# Revit family: Воздухоудалитель с функцией  выпуска воздуха 2630 10
name_source: partatom
category: Rohrzubehör
units: mm (PartAtom-declared; Revit-internal decimal feet)

## family parameters
Arbeitsebenenbasiert = Nein
Beim Laden mit Abzugskörper schneiden = Nein
Bemaßung runder Anschluss = Durchmesser verwenden
Gemeinsam genutzt = Nein
Immer vertikal = Ja
OmniClass-Nummer = 23.65.55.14
OmniClass-Titel = Valves for Liquid Services
Teiletyp = Normal

## types (1)
- Воздухоудалитель с функцией  выпуска воздуха 2630 10
    D01 = 17.8 mm  [stored 0.0583989 ft]
    D02 = 20 mm  [stored 0.0656168 ft]
    D03 = 11 mm  [stored 0.0360892 ft]
    D04 = 12.5 mm  [stored 0.0410105 ft]
    D05 = 5.1 mm  [stored 0.0167323 ft]
    D06 = 3.4 mm  [stored 0.0111549 ft]
    H00 = 56 mm  [stored 0.183727 ft]
    H01 = 9.5 mm  [stored 0.031168 ft]
    H02 = 13 mm
    H03 = 15.5 mm  [stored 0.050853 ft]
    H04 = 14.5 mm  [stored 0.0475722 ft]
    H05 = 9 mm  [stored 0.0295276 ft]
    H06 = 2.5 mm  [stored 0.0082021 ft]
    H07 = 48.5 mm
    H08 = 55 mm  [stored 0.180446 ft]
    Hersteller = Herz-Armaturen GmbH
    L01 = 4 mm  [stored 0.0131234 ft]
    L02 = 28.3 mm  [stored 0.0928478 ft]
    L03 = 9.5 mm  [stored 0.031168 ft]
    L04 = 18.8 mm  [stored 0.0616798 ft]
    R01 = 1 mm  [stored 0.00328084 ft]
    R02 = 0.6 mm  [stored 0.0019685 ft]
    S01 = 56 mm  [stored 0.183727 ft]
    S02 = 11 mm  [stored 0.0360892 ft]
    S03 = 24.5 mm  [stored 0.0803806 ft]
    SCRNCODE = 05;14;01
    SCRNSEQ = AWI;AWI_TYP="1013";1
    URL = www.herz-armaturen.ru
    Vorgabe-Ansicht = 0 mm  [stored 0 ft]
    Колпачок = ABS пластик, цвет красный
    Корпус = штампованная латунь в соответствии с EN 12165, CW617N
    Крышка корпуса = штампованная латунь в соответствии с EN 12165, CW617N
    Макс. давление на корпусе = 1000000.0 Pa
    Макс. рабочая температура = 110 °C
    Макс. рабочее давление = 1000000.0 Pa
    Мин. рабочая температура = 0 °C
    Наружная резьба подключения = в соответствии с ISO 228
    Область применения = Воздухоотводчик используется для удаления воздуха в системах отопления и холодоснабжения. Клапаны должны быть размещены рядом с котлом или же в самых высоких точках системы, чтобы обеспечить удаление воздуха из системы.
    Поплавок = Полипропилен
    Среда = Качество  теплоносителя в соответствии с ÖNORM H5195 и/или предписаниями VDI-Standard 2035.
Разрешается использование смеси этилен или пропиленгликоля в соотношении 25-50% с водой. Прокладки EPDM могут быть подвержены воздействию минеральных смазочных масел, что может служить причиной выхода из строя данных уплотнений. Пожалуйста, обратитесь к документации производителя, при использовании этиленгликоля и пропиленгликоля в целях защиты от замерзания.
    Уплотнение = EPDM

note: [stored X ft] marks values corroborated as IEEE doubles in the binary element streams (Revit-internal decimal feet)
